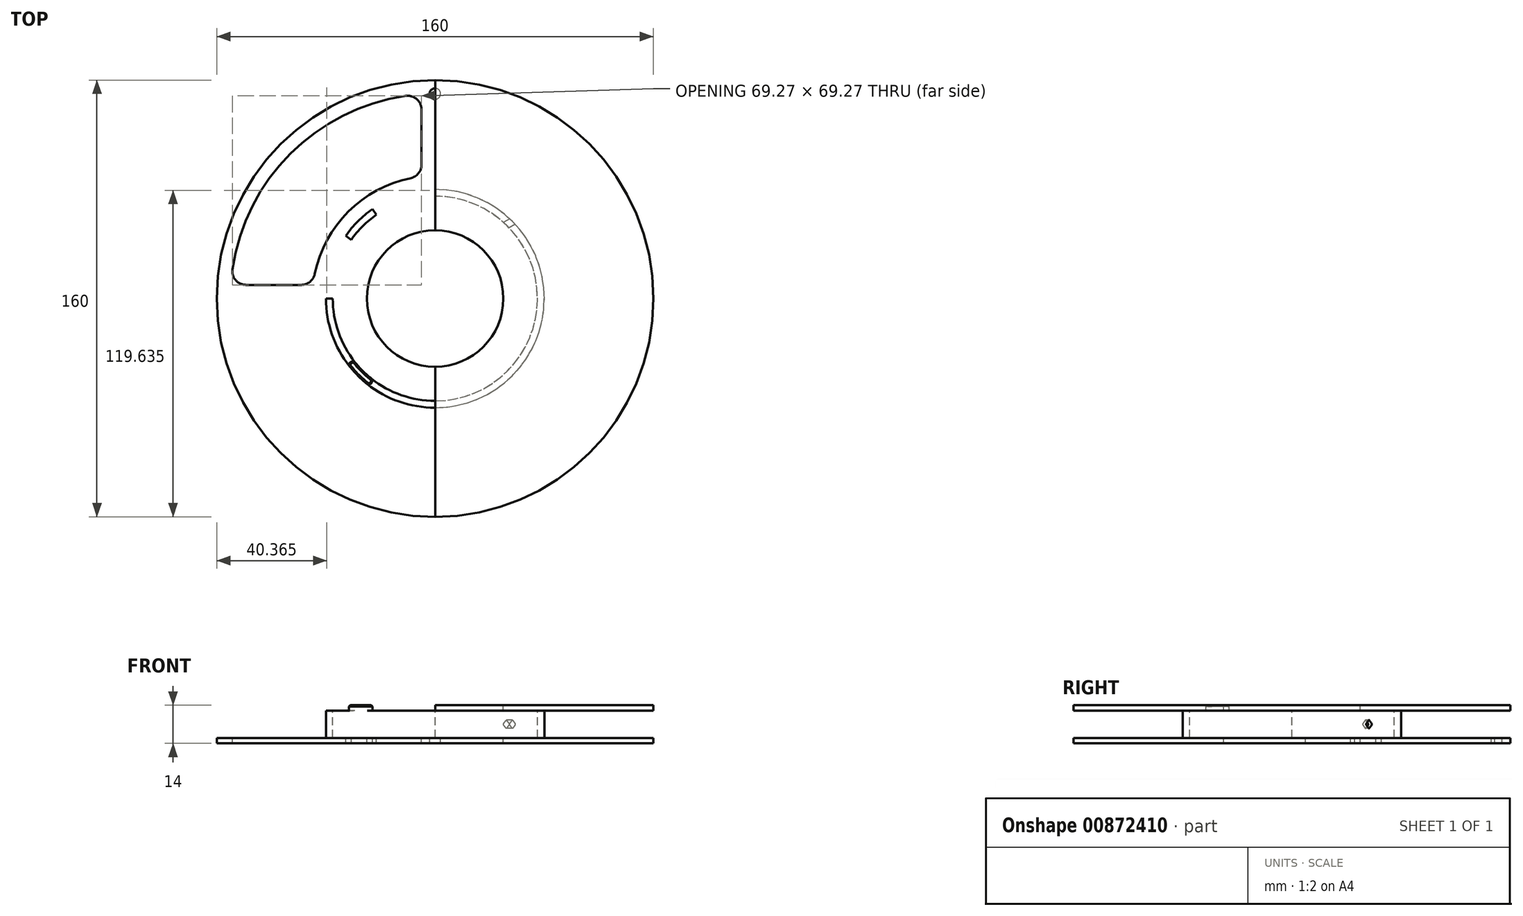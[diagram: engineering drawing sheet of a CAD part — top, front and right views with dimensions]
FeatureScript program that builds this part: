
annotation { "Feature Type Name" : "Feature", "Feature Type Description" : "" }
export const myFeature = defineFeature(function(context is Context, id is Id, definition is map)
    precondition{}
    {
        {
            var Q0;
            Q0=qCreatedBy(makeId("Front.planeOp"),FACE);
            var sketch = newSketch(context, id + "F0", { "sketchPlane" : qUnion([Q0])});
            skLineSegment(sketch, "E0", {"start": v(0, 7) * mm, "end": v(-80, 7) * mm});
            skLineSegment(sketch, "E1", {"start": v(-80, 7) * mm, "end": v(-80, 5) * mm});
            skLineSegment(sketch, "E2", {"start": v(-80, 5) * mm, "end": v(-40, 5) * mm});
            skLineSegment(sketch, "E3", {"start": v(-40, 5) * mm, "end": v(-40, 0) * mm});
            skLineSegment(sketch, "E4", {"start": v(-37.5, 0) * mm, "end": v(-37.5, 5) * mm});
            skLineSegment(sketch, "E5", {"start": v(-37.5, 5) * mm, "end": v(0, 5) * mm});
            skLineSegment(sketch, "E6", {"start": v(0, 5) * mm, "end": v(0, 7) * mm});
            skLineSegment(sketch, "E7.MirrorCS", {"start": v(-80, -7) * mm, "end": v(-80, -5) * mm});
            skLineSegment(sketch, "E8.MirrorCS", {"start": v(0, -7) * mm, "end": v(-80, -7) * mm});
            skLineSegment(sketch, "E9.MirrorCS", {"start": v(-80, -5) * mm, "end": v(-40, -5) * mm});
            skLineSegment(sketch, "E10.MirrorCS", {"start": v(-40, -5) * mm, "end": v(-40, 0) * mm});
            skLineSegment(sketch, "E11.MirrorCS", {"start": v(-37.5, 0) * mm, "end": v(-37.5, -5) * mm});
            skLineSegment(sketch, "E12.MirrorCS", {"start": v(-37.5, -5) * mm, "end": v(0, -5) * mm});
            skLineSegment(sketch, "E13.MirrorCS", {"start": v(0, -5) * mm, "end": v(0, -7) * mm});
            skLineSegment(sketch, "E14", {"start": v(0, 7) * mm, "end": v(0, -7) * mm, "construction": true});
            skSolve(sketch);
        }
        {
            var Q0;
            Q0=qSketchRegion(id+"F0",true);
            var Q1;
            Q1=sQuery(id+"F0.wireOp",EDGE,"E14");
            revolve(context, id + "F1", {"entities" : qUnion([Q0]), "axis" : qUnion([Q1]), "revolveType" : RevolveType.FULL});
        }
        {
            var Q0;
            Q0=makeQuery(id+"F1.opRevolve","SWEPT_FACE",FACE,{"disambiguationData":[OSD([sQuery(id+"F0.wireOp",EDGE,"E0")])]});
            var sketch = newSketch(context, id + "F2", { "sketchPlane" : qUnion([Q0])});
            skLineSegment(sketch, "E15", {"start": v(-40, 0) * mm, "end": v(-80, 0) * mm, "construction": true});
            skPoint(sketch, "E16.orphan", {"position": v(80, 0) * mm});
            skPoint(sketch, "E17.0.start.orphan", {"position": v(0, -80) * mm});
            skArc(sketch, "E18.0", {"start": v(0, 40) * mm, "mid": v(-28.28, 28.28) * mm, "end": v(-40, 0) * mm, "construction": true});
            skArc(sketch, "E19.1", {"start": v(-9, 44.1) * mm, "mid": v(-31.82, 31.82) * mm, "end": v(-44.1, 9) * mm});
            skLineSegment(sketch, "E20", {"start": v(0, 80) * mm, "end": v(0, 40) * mm, "construction": true});
            skPoint(sketch, "E21.visualSharp", {"position": v(-44.72, 5) * mm});
            skArc(sketch, "E21.filletArc", {"start": v(-48.99, 5) * mm, "mid": v(-45.83, 6.13) * mm, "end": v(-44.1, 9) * mm});
            skPoint(sketch, "E22.visualSharp", {"position": v(-73.21, 5) * mm});
            skPoint(sketch, "E23.visualSharp", {"position": v(-5, 73.21) * mm});
            skPoint(sketch, "E24.visualSharp", {"position": v(-5, 44.72) * mm});
            skArc(sketch, "E24.filletArc", {"start": v(-9, 44.1) * mm, "mid": v(-6.13, 45.83) * mm, "end": v(-5, 48.99) * mm});
            skArc(sketch, "E25", {"start": v(0, 80) * mm, "mid": v(-56.57, 56.57) * mm, "end": v(-80, 0) * mm, "construction": true});
            skArc(sketch, "E26.0", {"start": v(-10.71, 74.23) * mm, "mid": v(-53.03, 53.03) * mm, "end": v(-74.23, 10.71) * mm});
            skLineSegment(sketch, "E27", {"start": v(-48.99, 5) * mm, "end": v(-69.28, 5) * mm});
            skLineSegment(sketch, "E28", {"start": v(-5, 48.99) * mm, "end": v(-5, 69.28) * mm});
            skArc(sketch, "E29.filletArc", {"start": v(-5, 69.28) * mm, "mid": v(-6.73, 73.06) * mm, "end": v(-10.71, 74.23) * mm});
            skArc(sketch, "E30.filletArc", {"start": v(-74.23, 10.71) * mm, "mid": v(-73.06, 6.73) * mm, "end": v(-69.28, 5) * mm});
            skSolve(sketch);
        }
        {
            var Q0;
            Q0=qSketchRegion(id+"F2",true);
            extrude(context, id + "F3", {"entities" : qUnion([Q0]), "operationType" : NewBodyOperationType.REMOVE, "endBound" : BoundingType.THROUGH_ALL, "oppositeDirection" : true, "depth" : 25 * mm});
        }
        {
            var Q0;
            Q0=sQuery(id+"F2.wireOp",VERTEX,"E18.0.center");
            var Q1;
            Q1=makeQuery(id+"F1.opRevolve","SWEPT_BODY",BODY,{"disambiguationData":[OSD([sQuery(id+"F0.wireOp",EDGE,"E0"),sQuery(id+"F0.wireOp",EDGE,"E1"),sQuery(id+"F0.wireOp",EDGE,"E2"),sQuery(id+"F0.wireOp",EDGE,"E3"),sQuery(id+"F0.wireOp",EDGE,"E4"),sQuery(id+"F0.wireOp",EDGE,"E5"),sQuery(id+"F0.wireOp",EDGE,"E6"),sQuery(id+"F0.wireOp",EDGE,"E7.MirrorCS"),sQuery(id+"F0.wireOp",EDGE,"E8.MirrorCS"),sQuery(id+"F0.wireOp",EDGE,"E9.MirrorCS"),sQuery(id+"F0.wireOp",EDGE,"E10.MirrorCS"),sQuery(id+"F0.wireOp",EDGE,"E11.MirrorCS"),sQuery(id+"F0.wireOp",EDGE,"E12.MirrorCS"),sQuery(id+"F0.wireOp",EDGE,"E13.MirrorCS")])]});
            hole(context, id + "F4", {"style" : HoleStyle.SIMPLE, "endStyle" : HoleEndStyle.THROUGH, "holeDiameter" : 50 * mm, "majorDiameter" : 5 * mm, "isTappedThrough" : true, "tappedDepth" : 38.4 * mm, "tapClearance" : 3, "locations" : qUnion([Q0]), "scope" : qUnion([Q1])});
        }
        {
            var Q0;
            Q0=makeQuery(id+"F2.imprint","IMPRINT",FACE,{"disambiguationData":[TD([[makeQuery(id+"F2.imprint","IMPRINT",EDGE,{"derivedFrom":sQuery(id+"F2.wireOp",EDGE,"E19.1")}),1.0]])]});
            var sketch = newSketch(context, id + "F5", { "sketchPlane" : qUnion([Q0])});
            skLineSegment(sketch, "E31", {"start": v(0, 80) * mm, "end": v(0, 0) * mm});
            skLineSegment(sketch, "E32", {"start": v(0, 0) * mm, "end": v(-80, 0) * mm});
            skLineSegment(sketch, "E33", {"start": v(-80, 0) * mm, "end": v(-80, 80) * mm});
            skLineSegment(sketch, "E34", {"start": v(-80, 80) * mm, "end": v(0, 80) * mm});
            skSolve(sketch);
        }
        {
            var Q0;
            Q0=qSketchRegion(id+"F5",true);
            var Q1;
            Q1=makeQuery(id+"F1.opRevolve","SWEPT_FACE",FACE,{"disambiguationData":[OSD([sQuery(id+"F0.wireOp",EDGE,"E9.MirrorCS")])]});
            extrude(context, id + "F6", {"entities" : qUnion([Q0]), "operationType" : NewBodyOperationType.REMOVE, "endBound" : BoundingType.UP_TO_SURFACE, "oppositeDirection" : true, "endBoundEntityFace" : qUnion([Q1]), "depth" : 25 * mm});
        }
        {
            var Q0;
            Q0=qCreatedBy(makeId("Right.planeOp"),FACE);
            var sketch = newSketch(context, id + "F7", { "sketchPlane" : qUnion([Q0])});
            skPoint(sketch, "E35.0", {"position": v(80, 7) * mm});
            skPoint(sketch, "E36.0", {"position": v(-80, 5) * mm});
            skLineSegment(sketch, "E37.bottom", {"start": v(-80, 5) * mm, "end": v(80, 5) * mm, "construction": true});
            skLineSegment(sketch, "E37.top", {"start": v(-80, 7) * mm, "end": v(80, 7) * mm, "construction": true});
            skLineSegment(sketch, "E37.left", {"start": v(-80, 5) * mm, "end": v(-80, 7) * mm, "construction": true});
            skLineSegment(sketch, "E37.right", {"start": v(80, 5) * mm, "end": v(80, 7) * mm, "construction": true});
            skLineSegment(sketch, "E38.bottom", {"start": v(80, 7) * mm, "end": v(-80, 7) * mm});
            skLineSegment(sketch, "E38.top", {"start": v(80, 5) * mm, "end": v(-80, 5) * mm});
            skLineSegment(sketch, "E38.left", {"start": v(80, 7) * mm, "end": v(80, 5) * mm});
            skLineSegment(sketch, "E38.right", {"start": v(-80, 7) * mm, "end": v(-80, 5) * mm});
            skSolve(sketch);
        }
        {
            var Q0;
            Q0=qSketchRegion(id+"F7",true);
            extrude(context, id + "F8", {"entities" : qUnion([Q0]), "operationType" : NewBodyOperationType.REMOVE, "endBound" : BoundingType.THROUGH_ALL, "oppositeDirection" : true, "depth" : 25 * mm});
        }
        {
            var Q0;
            {var subQ0=sQuery(id+"F0.wireOp",EDGE,"E12.MirrorCS");var subQ1=sQuery(id+"F0.wireOp",EDGE,"E9.MirrorCS");Q0=makeQuery(id+"F5vmHWThCkjWJyu_1.1.F6.boolean.opBoolean","MERGE",FACE,{"derivedFrom":[makeQuery(id+"F6.boolean.opBoolean","MERGE",FACE,{"derivedFrom":[makeQuery(id+"F1.opRevolve","SWEPT_FACE",FACE,{"disambiguationData":[OSD([subQ1])]}),makeQuery(id+"F1.opRevolve","SWEPT_FACE",FACE,{"disambiguationData":[OSD([subQ0])]}),makeQuery(id+"F6.opExtrude","CAP_FACE",FACE,{"disambiguationData":[OSD([subQ1])],"isStart":false})]}),makeQuery(id+"F5vmHWThCkjWJyu_1.1.F6.opExtrude","CAP_FACE",FACE,{"disambiguationData":[OSD([subQ1,subQ0])],"isStart":false})]});}
            var sketch = newSketch(context, id + "F9", { "sketchPlane" : qUnion([Q0])});
            skArc(sketch, "E39.0", {"start": v(0, 40) * mm, "mid": v(-28.28, 28.28) * mm, "end": v(-40, 0) * mm, "construction": true});
            skLineSegment(sketch, "E40", {"start": v(0, 0) * mm, "end": v(-28.28, 28.28) * mm, "construction": true});
            skArc(sketch, "E41", {"start": v(-28.28, 28.28) * mm, "mid": v(-25.71, 30.64) * mm, "end": v(-22.94, 32.77) * mm});
            skArc(sketch, "E42.0", {"start": v(37.5, 0) * mm, "mid": v(26.52, 26.52) * mm, "end": v(0, 37.5) * mm, "construction": true});
            skArc(sketch, "E43", {"start": v(0, 37.5) * mm, "mid": v(-26.52, 26.52) * mm, "end": v(-37.5, 0) * mm, "construction": true});
            skLineSegment(sketch, "E44", {"start": v(-22.94, 32.77) * mm, "end": v(0, 0) * mm, "construction": true});
            skArc(sketch, "E45", {"start": v(-26.52, 26.52) * mm, "mid": v(-24.1, 28.73) * mm, "end": v(-21.5, 30.72) * mm});
            skArc(sketch, "E46.MirrorCS", {"start": v(-37.5, 0) * mm, "mid": v(-26.52, 26.52) * mm, "end": v(0, 37.5) * mm, "construction": true});
            skArc(sketch, "E47.MirrorCS", {"start": v(-40, 0) * mm, "mid": v(-28.28, 28.28) * mm, "end": v(0, 40) * mm, "construction": true});
            skArc(sketch, "E48", {"start": v(-32.77, 22.94) * mm, "mid": v(-30.64, 25.71) * mm, "end": v(-28.28, 28.28) * mm});
            skLineSegment(sketch, "E49", {"start": v(-32.77, 22.94) * mm, "end": v(0, 0) * mm, "construction": true});
            skArc(sketch, "E50", {"start": v(-30.72, 21.5) * mm, "mid": v(-28.73, 24.1) * mm, "end": v(-26.52, 26.52) * mm});
            skLineSegment(sketch, "E51", {"start": v(-30.72, 21.5) * mm, "end": v(-32.77, 22.94) * mm});
            skLineSegment(sketch, "E52", {"start": v(-22.94, 32.77) * mm, "end": v(-21.5, 30.72) * mm});
            skSolve(sketch);
        }
        {
            var Q0;
            Q0=qSketchRegion(id+"F9",true);
            extrude(context, id + "F10", {"entities" : qUnion([Q0]), "operationType" : NewBodyOperationType.REMOVE, "endBound" : BoundingType.THROUGH_ALL, "oppositeDirection" : true, "depth" : 25 * mm});
        }
        {
            var Q0;
            Q0=makeQuery(id+"F2.imprint","IMPRINT",FACE,{"disambiguationData":[TD([[makeQuery(id+"F2.imprint","IMPRINT",EDGE,{"derivedFrom":sQuery(id+"F2.wireOp",EDGE,"E19.1")}),1.0]])]});
            var sketch = newSketch(context, id + "F11", { "sketchPlane" : qUnion([Q0])});
            skArc(sketch, "E53.0", {"start": v(-37.5, 0) * mm, "mid": v(-26.52, -26.52) * mm, "end": v(0, -37.5) * mm, "construction": true});
            skArc(sketch, "E54.0", {"start": v(-40, 0) * mm, "mid": v(-28.28, -28.28) * mm, "end": v(0, -40) * mm, "construction": true});
            skLineSegment(sketch, "E55", {"start": v(-28.28, -28.28) * mm, "end": v(0, 0) * mm, "construction": true});
            skLineSegment(sketch, "E56", {"start": v(-24.07, -31.95) * mm, "end": v(0, 0) * mm, "construction": true});
            skLineSegment(sketch, "E57", {"start": v(-31.95, -24.07) * mm, "end": v(0, 0) * mm, "construction": true});
            skArc(sketch, "E58", {"start": v(-24.07, -31.95) * mm, "mid": v(-28.28, -28.28) * mm, "end": v(-31.95, -24.07) * mm});
            skArc(sketch, "E59", {"start": v(-22.57, -29.95) * mm, "mid": v(-26.52, -26.52) * mm, "end": v(-29.95, -22.57) * mm});
            skLineSegment(sketch, "E60", {"start": v(-31.95, -24.07) * mm, "end": v(-29.95, -22.57) * mm});
            skLineSegment(sketch, "E61", {"start": v(-22.57, -29.95) * mm, "end": v(-24.07, -31.95) * mm});
            skSolve(sketch);
        }
        {
            var Q0;
            Q0=qSketchRegion(id+"F11",true);
            var Q1;
            Q1=makeQuery(id+"F8.boolean.opBoolean","COPY",FACE,{"derivedFrom":makeQuery(id+"F8.opExtrude","SWEPT_FACE",FACE,{"disambiguationData":[OSD([sQuery(id+"F7.wireOp",EDGE,"E38.top")])]})});
            extrude(context, id + "F12", {"entities" : qUnion([Q0]), "operationType" : NewBodyOperationType.ADD, "endBound" : BoundingType.UP_TO_SURFACE, "oppositeDirection" : true, "endBoundEntityFace" : qUnion([Q1]), "depth" : 25 * mm});
        }
        {
            var Q0;
            Q0=makeQuery(id+"F12.opExtrude","SWEPT_EDGE",EDGE,{"disambiguationData":[OSD([sQuery(id+"F11.wireOp",EDGE,"E58"),sQuery(id+"F11.wireOp",EDGE,"E60")])]});
            var Q1;
            Q1=makeQuery(id+"F12.opExtrude","SWEPT_EDGE",EDGE,{"disambiguationData":[OSD([sQuery(id+"F11.wireOp",EDGE,"E58"),sQuery(id+"F11.wireOp",EDGE,"E61")])]});
            var Q2;
            Q2=makeQuery(id+"F12.opExtrude","SWEPT_EDGE",EDGE,{"disambiguationData":[OSD([sQuery(id+"F11.wireOp",EDGE,"E59"),sQuery(id+"F11.wireOp",EDGE,"E60")])]});
            var Q3;
            Q3=makeQuery(id+"F12.opExtrude","SWEPT_EDGE",EDGE,{"disambiguationData":[OSD([sQuery(id+"F11.wireOp",EDGE,"E59"),sQuery(id+"F11.wireOp",EDGE,"E61")])]});
            fillet(context, id + "F13", {"entities" : qUnion([Q0, Q1, Q2, Q3]), "radius" : 1 * mm, "tangentPropagation" : true, "allowEdgeOverflow" : false});
        }
        {
            var Q0;
            Q0=makeQuery(id+"F12.opExtrude","CAP_EDGE",EDGE,{"disambiguationData":[OSD([sQuery(id+"F11.wireOp",EDGE,"E58")])],"isStart":true});
            var Q1;
            Q1=makeQuery(id+"F12.opExtrude","CAP_EDGE",EDGE,{"disambiguationData":[OSD([sQuery(id+"F11.wireOp",EDGE,"E59")])],"isStart":true});
            var Q2;
            Q2=makeQuery(id+"F12.opExtrude","CAP_EDGE",EDGE,{"disambiguationData":[OSD([sQuery(id+"F11.wireOp",EDGE,"E61")])],"isStart":true});
            var Q3;
            Q3=makeQuery(id+"F12.opExtrude","CAP_EDGE",EDGE,{"disambiguationData":[OSD([sQuery(id+"F11.wireOp",EDGE,"E60")])],"isStart":true});
            var Q4;
            Q4=makeQuery(id+"F10.boolean.opBoolean","COPY",EDGE,{"derivedFrom":makeQuery(id+"F10.opExtrude","CAP_EDGE",EDGE,{"disambiguationData":[OSD([sQuery(id+"F9.wireOp",EDGE,"E45"),sQuery(id+"F9.wireOp",EDGE,"E50")])],"isStart":true})});
            var Q5;
            Q5=makeQuery(id+"F10.boolean.opBoolean","COPY",EDGE,{"derivedFrom":makeQuery(id+"F10.opExtrude","CAP_EDGE",EDGE,{"disambiguationData":[OSD([sQuery(id+"F9.wireOp",EDGE,"E51")])],"isStart":true})});
            var Q6;
            Q6=makeQuery(id+"F10.boolean.opBoolean","COPY",EDGE,{"derivedFrom":makeQuery(id+"F10.opExtrude","CAP_EDGE",EDGE,{"disambiguationData":[OSD([sQuery(id+"F9.wireOp",EDGE,"E41"),sQuery(id+"F9.wireOp",EDGE,"E48")])],"isStart":true})});
            var Q7;
            Q7=makeQuery(id+"F10.boolean.opBoolean","COPY",EDGE,{"derivedFrom":makeQuery(id+"F10.opExtrude","CAP_EDGE",EDGE,{"disambiguationData":[OSD([sQuery(id+"F9.wireOp",EDGE,"E52")])],"isStart":true})});
            chamfer(context, id + "F14", {"entities" : qUnion([Q0, Q1, Q2, Q3, Q4, Q5, Q6, Q7]), "width" : .5 * mm, "tangentPropagation" : true});
        }
        {
            var Q0;
            Q0=sQuery(id+"F0.wireOp",EDGE,"E14");
            var Q1;
            Q1=qCreatedBy(makeId("Right.planeOp"),FACE);
            cPlane(context, id + "F15", {"entities" : qUnion([Q0, Q1]), "cplaneType" : CPlaneType.LINE_ANGLE, "offset" : 25 * mm, "angle" : 330 * degree, "width" : 150 * mm, "height" : 150 * mm});
        }
        {
            var Q0;
            Q0=qCreatedBy(id+"F15.planeOp",FACE);
            var sketch = newSketch(context, id + "F16", { "sketchPlane" : qUnion([Q0])});
            skLineSegment(sketch, "E62", {"start": v(-11.51, 0.35) * mm, "end": v(-10.42, 1.44) * mm});
            skLineSegment(sketch, "E63", {"start": v(-10.14, 1.44) * mm, "end": v(-9.05, 0.35) * mm});
            skLineSegment(sketch, "E64", {"start": v(-9.05, -0.35) * mm, "end": v(-10.14, -1.44) * mm});
            skLineSegment(sketch, "E65", {"start": v(-10.42, -1.44) * mm, "end": v(-11.51, -0.35) * mm});
            skPoint(sketch, "E66.visualSharp", {"position": v(-11.87, 0) * mm});
            skArc(sketch, "E66.filletArc", {"start": v(-11.51, 0.35) * mm, "mid": v(-11.66, 0) * mm, "end": v(-11.51, -0.35) * mm});
            skPoint(sketch, "E67.visualSharp", {"position": v(-10.28, -1.59) * mm});
            skArc(sketch, "E67.filletArc", {"start": v(-10.42, -1.44) * mm, "mid": v(-10.28, -1.5) * mm, "end": v(-10.14, -1.44) * mm});
            skPoint(sketch, "E68.visualSharp", {"position": v(-8.7, 0) * mm});
            skArc(sketch, "E68.filletArc", {"start": v(-9.05, -0.35) * mm, "mid": v(-8.9, 0) * mm, "end": v(-9.05, 0.35) * mm});
            skPoint(sketch, "E69.visualSharp", {"position": v(-10.28, 1.59) * mm});
            skArc(sketch, "E69.filletArc", {"start": v(-10.14, 1.44) * mm, "mid": v(-10.28, 1.5) * mm, "end": v(-10.42, 1.44) * mm});
            skSolve(sketch);
        }
        {
            var Q0;
            Q0=makeQuery(id+"F16.imprint","IMPRINT",FACE,{"disambiguationData":[TD([[makeQuery(id+"F16.imprint","IMPRINT",EDGE,{"derivedFrom":sQuery(id+"F16.wireOp",EDGE,"E62")}),-1.0]])]});
            extrude(context, id + "F17", {"entities" : qUnion([Q0]), "operationType" : NewBodyOperationType.REMOVE, "endBound" : BoundingType.THROUGH_ALL, "oppositeDirection" : true, "depth" : 25 * mm});
        }
        {
            var Q0;
            Q0=qCreatedBy(makeId("Top.planeOp"),FACE);
            var sketch = newSketch(context, id + "F18", { "sketchPlane" : qUnion([Q0])});
            skLineSegment(sketch, "E70", {"start": v(0, 87.17) * mm, "end": v(0, 0) * mm, "construction": true});
            skPoint(sketch, "E71", {"position": v(0, 75) * mm});
            skSolve(sketch);
        }
        {
            var Q0;
            Q0=sQuery(id+"F18.wireOp",VERTEX,"E71");
            var Q1;
            Q1=makeQuery(id+"F1.opRevolve","SWEPT_BODY",BODY,{"disambiguationData":[OSD([sQuery(id+"F0.wireOp",EDGE,"E0"),sQuery(id+"F0.wireOp",EDGE,"E1"),sQuery(id+"F0.wireOp",EDGE,"E2"),sQuery(id+"F0.wireOp",EDGE,"E3"),sQuery(id+"F0.wireOp",EDGE,"E4"),sQuery(id+"F0.wireOp",EDGE,"E5"),sQuery(id+"F0.wireOp",EDGE,"E6"),sQuery(id+"F0.wireOp",EDGE,"E7.MirrorCS"),sQuery(id+"F0.wireOp",EDGE,"E8.MirrorCS"),sQuery(id+"F0.wireOp",EDGE,"E9.MirrorCS"),sQuery(id+"F0.wireOp",EDGE,"E10.MirrorCS"),sQuery(id+"F0.wireOp",EDGE,"E11.MirrorCS"),sQuery(id+"F0.wireOp",EDGE,"E12.MirrorCS"),sQuery(id+"F0.wireOp",EDGE,"E13.MirrorCS")])]});
            hole(context, id + "F19", {"style" : HoleStyle.SIMPLE, "endStyle" : HoleEndStyle.THROUGH, "holeDiameter" : 4 * mm, "isTappedThrough" : true, "tappedDepth" : 38.4 * mm, "tapClearance" : 3, "locations" : qUnion([Q0]), "scope" : qUnion([Q1])});
        }
    });
